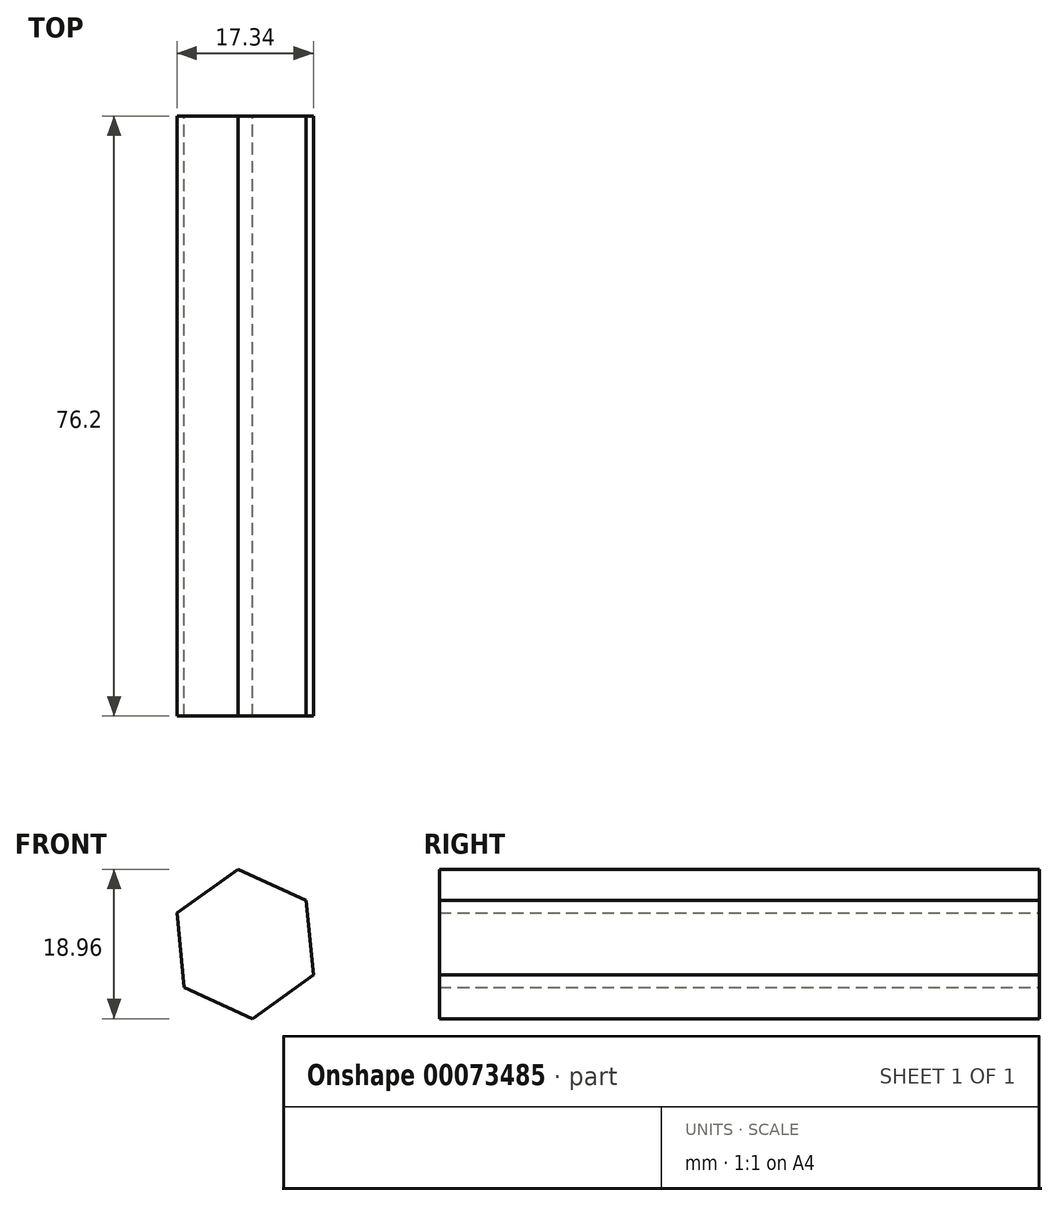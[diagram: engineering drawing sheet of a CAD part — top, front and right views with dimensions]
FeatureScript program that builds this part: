
annotation { "Feature Type Name" : "Feature", "Feature Type Description" : "" }
export const myFeature = defineFeature(function(context is Context, id is Id, definition is map)
    precondition{}
    {
        {
            var Q0;
            Q0=qCreatedBy(makeId("Front.planeOp"),FACE);
            var sketch = newSketch(context, id + "F0", { "sketchPlane" : qUnion([Q0])});
            skCircle(sketch, "E0.cCircle", {"center": v(-12.84, 19.26) * mm, "radius": 8.25 * mm, "construction": true});
            skLineSegment(sketch, "E0.0", {"start": v(-4.17, 15.32) * mm, "end": v(-11.92, 9.78) * mm});
            skLineSegment(sketch, "E0.1", {"start": v(-11.92, 9.78) * mm, "end": v(-20.6, 13.73) * mm});
            skLineSegment(sketch, "E0.2", {"start": v(-20.6, 13.73) * mm, "end": v(-21.51, 23.2) * mm});
            skLineSegment(sketch, "E0.3", {"start": v(-21.51, 23.2) * mm, "end": v(-13.76, 28.74) * mm});
            skLineSegment(sketch, "E0.4", {"start": v(-13.76, 28.74) * mm, "end": v(-5.1, 24.8) * mm});
            skLineSegment(sketch, "E0.5", {"start": v(-5.1, 24.8) * mm, "end": v(-4.17, 15.32) * mm});
            skPoint(sketch, "E0.0.midPoint", {"position": v(-8.05, 12.55) * mm});
            skSolve(sketch);
        }
        {
            var Q0;
            Q0=makeQuery(id+"F0.imprint","IMPRINT",FACE,{"disambiguationData":[TD([[makeQuery(id+"F0.imprint","IMPRINT",EDGE,{"derivedFrom":sQuery(id+"F0.wireOp",EDGE,"E0.0")}),-1.0]])]});
            extrude(context, id + "F1", {"entities" : qUnion([Q0]), "depth" : 76.2 * mm});
        }
    });
